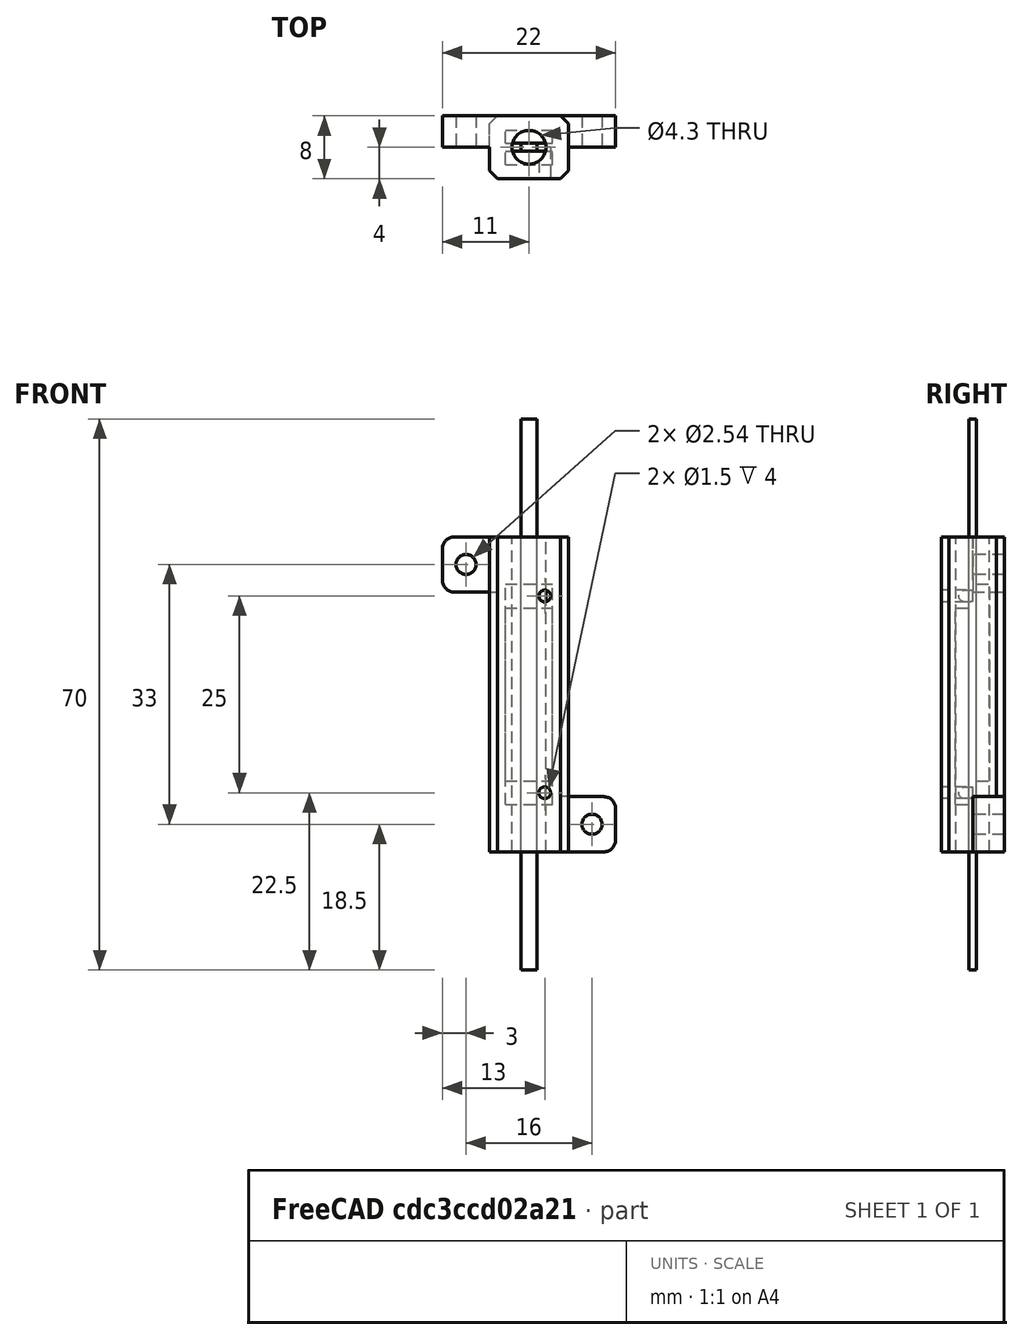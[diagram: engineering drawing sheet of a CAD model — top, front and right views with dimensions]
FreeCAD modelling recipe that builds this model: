
FCSTD DOCUMENT  (FreeCAD 0.14R3702 (Git))
Label: er-valve
License: CC-BY 3.0
LicenseURL: http://creativecommons.org/licenses/by/3.0/
objects: Part::Box×6, Part::Cylinder×5, Part::Cut×5, Part::Chamfer×4, Part::Fillet×4, Part::Fuse×2
note: 26 computed .brp shape members not serialized (recipe doc carries the construction recipe); baked Part::Feature solids carry a one-line shape summary decoded from their .brp

FEATURE [Part::Box] Box  label="Cube"
  Height = 70
  Length = 2
  Placement = pos=(-1,-0.5,-35) rot=(0,0,1;0rad)
  Width = 1
FEATURE [Part::Cylinder] Cylinder
  Angle = 360
  Height = 60
  Placement = pos=(0,0,-30) rot=(0,0,1;0rad)
  Radius = 2.15
FEATURE [Part::Box] Box001  label="Cube001"
  Height = 40
  Length = 10
  Placement = pos=(-5,-4,-20) rot=(0,0,1;0rad)
  Width = 8
FEATURE [Part::Box] Box002  label="Cube002"
  Height = 25
  Length = 6
  Placement = pos=(-3,-2.2,-14) rot=(0,0,1;0rad)
  Width = 1.7
FEATURE [Part::Box] Box003  label="Cube003"
  Height = 25
  Length = 6
  Placement = pos=(-3,0.5,-11) rot=(0,0,1;0rad)
  Width = 1.7
FEATURE [Part::Cylinder] Cylinder001
  Angle = 360
  Height = 20
  Placement = pos=(2,0,12.5) rot=(1,0,0;1.5708rad)
  Radius = 0.75
FEATURE [Part::Cylinder] Cylinder002
  Angle = 360
  Height = 20
  Placement = pos=(2,0,-12.5) rot=(1,0,0;1.5708rad)
  Radius = 0.75
FEATURE [Part::Chamfer] Chamfer
  Base = -> Box001
  Edges = 1 edges r=1: [Edge1]
FEATURE [Part::Chamfer] Chamfer001
  Base = -> Chamfer
  Edges = 1 edges r=1: [Edge15]
FEATURE [Part::Chamfer] Chamfer002
  Base = -> Chamfer001
  Edges = 1 edges r=1: [Edge14]
FEATURE [Part::Chamfer] Chamfer003
  Base = -> Chamfer002
  Edges = 1 edges r=1: [Edge16]
FEATURE [Part::Cylinder] Cylinder003
  Angle = 360
  Height = 20
  Placement = pos=(-8,9,16.5) rot=(1,0,0;1.5708rad)
  Radius = 1.27
FEATURE [Part::Cylinder] Cylinder004
  Angle = 360
  Height = 20
  Placement = pos=(8,9,-16.5) rot=(1,0,0;1.5708rad)
  Radius = 1.27
FEATURE [Part::Box] Box004  label="Cube004"
  Height = 7
  Length = 8
  Placement = pos=(3,0,-20) rot=(0,0,1;0rad)
  Width = 4
FEATURE [Part::Box] Box005  label="Cube005"
  Height = 7
  Length = 8
  Placement = pos=(-11,0,13) rot=(0,0,1;0rad)
  Width = 4
FEATURE [Part::Fuse] Fusion
  Base = -> Chamfer003
  Tool = -> Box004
FEATURE [Part::Fuse] Fusion001
  Base = -> Box005
  Tool = -> Fusion
FEATURE [Part::Cut] Cut
  Base = -> Fusion001
  Tool = -> Cylinder004
FEATURE [Part::Cut] Cut001
  Base = -> Cut
  Tool = -> Cylinder003
FEATURE [Part::Fillet] Fillet
  Base = -> Cut001
  Edges = 1 edges r=1.5: [Edge2]
FEATURE [Part::Fillet] Fillet001
  Base = -> Fillet
  Edges = 1 edges r=1.5: [Edge3]
FEATURE [Part::Fillet] Fillet002
  Base = -> Fillet001
  Edges = 1 edges r=1.5: [Edge69]
FEATURE [Part::Fillet] Fillet003
  Base = -> Fillet002
  Edges = 1 edges r=1.5: [Edge18]
FEATURE [Part::Cut] Cut002
  Base = -> Fillet003
  Tool = -> Cylinder
FEATURE [Part::Cut] Cut003
  Base = -> Cut002
  Tool = -> Cylinder001
FEATURE [Part::Cut] Cut004
  Base = -> Cut003
  Tool = -> Cylinder002
